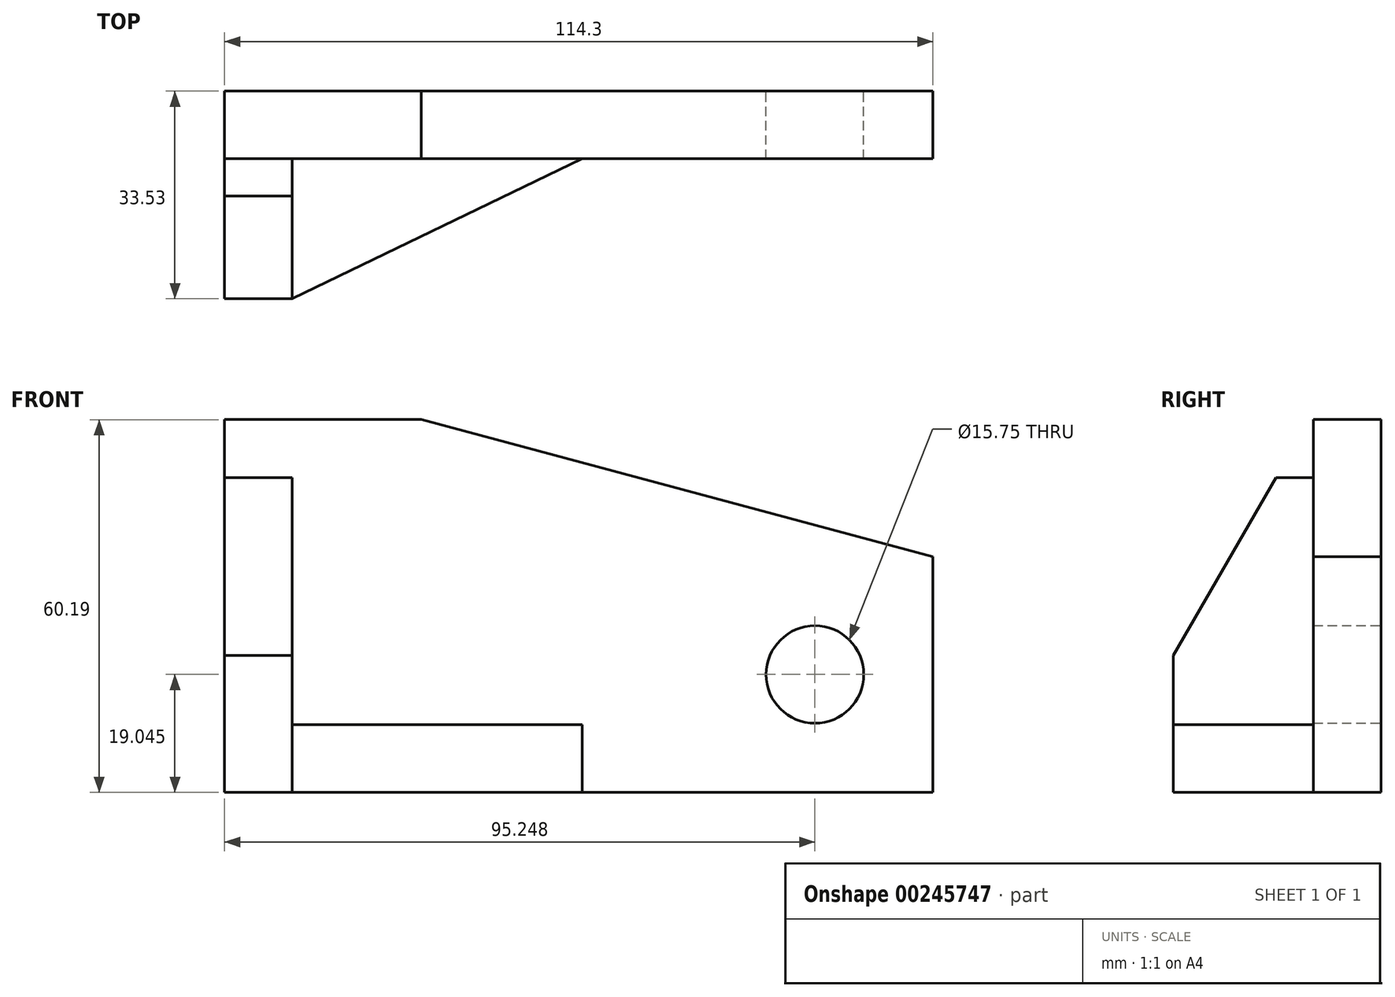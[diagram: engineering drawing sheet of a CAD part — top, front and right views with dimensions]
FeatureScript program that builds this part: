
annotation { "Feature Type Name" : "Feature", "Feature Type Description" : "" }
export const myFeature = defineFeature(function(context is Context, id is Id, definition is map)
    precondition{}
    {
        {
            var Q0;
            Q0=qCreatedBy(makeId("Front.planeOp"),FACE);
            var sketch = newSketch(context, id + "F0", { "sketchPlane" : qUnion([Q0])});
            skLineSegment(sketch, "E0.bottom", {"start": v(-75.62, 47.76) * mm, "end": v(-43.87, 47.76) * mm});
            skLineSegment(sketch, "E0.top", {"start": v(-75.62, -12.43) * mm, "end": v(-43.87, -12.43) * mm});
            skLineSegment(sketch, "E0.left", {"start": v(-75.62, 47.76) * mm, "end": v(-75.62, -12.43) * mm});
            skLineSegment(sketch, "E1", {"start": v(-43.87, -12.43) * mm, "end": v(38.68, -12.43) * mm});
            skLineSegment(sketch, "E2", {"start": v(-43.87, 47.76) * mm, "end": v(38.68, 25.64) * mm});
            skLineSegment(sketch, "E3", {"start": v(38.68, -12.43) * mm, "end": v(38.68, 25.64) * mm});
            skCircle(sketch, "E4", {"center": v(19.63, 6.62) * mm, "radius": 7.87 * mm});
            skLineSegment(sketch, "E5", {"start": v(-64.7, -1.51) * mm, "end": v(-12.12, -1.51) * mm});
            skLineSegment(sketch, "E6", {"start": v(-12.12, -1.51) * mm, "end": v(-12.12, -12.43) * mm});
            skLineSegment(sketch, "E7", {"start": v(-64.7, -12.43) * mm, "end": v(-64.7, 38.37) * mm});
            skLineSegment(sketch, "E8", {"start": v(-135.58, 18.97) * mm, "end": v(-64.7, 18.97) * mm});
            skLineSegment(sketch, "E9", {"start": v(-64.7, 38.37) * mm, "end": v(-75.62, 38.37) * mm});
            skSolve(sketch);
        }
        {
            var Q0;
            Q0=makeQuery(id+"F0.imprint","IMPRINT",FACE,{"disambiguationData":[TD([[makeQuery(id+"F0.imprint","IMPRINT",EDGE,{"derivedFrom":sQuery(id+"F0.wireOp",EDGE,"E0.bottom")}),-1.0]])]});
            extrude(context, id + "F1", {"entities" : qUnion([Q0]), "depth" : 10.92 * mm});
        }
        {
            var Q0;
            {var subQ1=sQuery(id+"F0.wireOp",EDGE,"E5");Q0=makeQuery(id+"F0.imprint","IMPRINT",FACE,{"disambiguationData":[TD([[makeQuery(id+"F0.imprint","IMPRINT",EDGE,{"derivedFrom":subQ1}),-1.0]])]});}
            extrude(context, id + "F2", {"entities" : qUnion([Q0]), "operationType" : NewBodyOperationType.ADD, "depth" : 33.53 * mm});
        }
        {
            var Q0;
            {var subQ1=sQuery(id+"F0.wireOp",EDGE,"E8");Q0=makeQuery(id+"F0.imprint","IMPRINT",FACE,{"disambiguationData":[TD([[makeQuery(id+"F0.imprint","IMPRINT",EDGE,{"derivedFrom":subQ1}),1.0]])]});}
            var Q1;
            {var subQ2=sQuery(id+"F0.wireOp",EDGE,"E8");Q1=makeQuery(id+"F0.imprint","IMPRINT",FACE,{"disambiguationData":[TD([[makeQuery(id+"F0.imprint","IMPRINT",EDGE,{"derivedFrom":subQ2}),-1.0]])]});}
            extrude(context, id + "F3", {"entities" : qUnion([Q0, Q1]), "operationType" : NewBodyOperationType.ADD, "depth" : 33.53 * mm});
        }
        {
            var Q0;
            Q0=makeQuery(id+"F3.opExtrude","CAP_EDGE",EDGE,{"disambiguationData":[OSD([sQuery(id+"F0.wireOp",EDGE,"E9")])],"isStart":false});
            chamfer(context, id + "F4", {"entities" : qUnion([Q0]), "chamferType" : ChamferType.OFFSET_ANGLE, "width" : 28.7 * mm, "oppositeDirection" : false, "angle" : 30 * degree, "tangentPropagation" : true});
        }
        {
            var Q0;
            Q0=makeQuery(id+"F2.opExtrude","CAP_EDGE",EDGE,{"disambiguationData":[OSD([sQuery(id+"F0.wireOp",EDGE,"E6")])],"isStart":false});
            chamfer(context, id + "F5", {"entities" : qUnion([Q0]), "chamferType" : ChamferType.TWO_OFFSETS, "width1" : 25.4 * mm, "oppositeDirection" : false, "width2" : 52.58 * mm, "tangentPropagation" : true});
        }
    });
